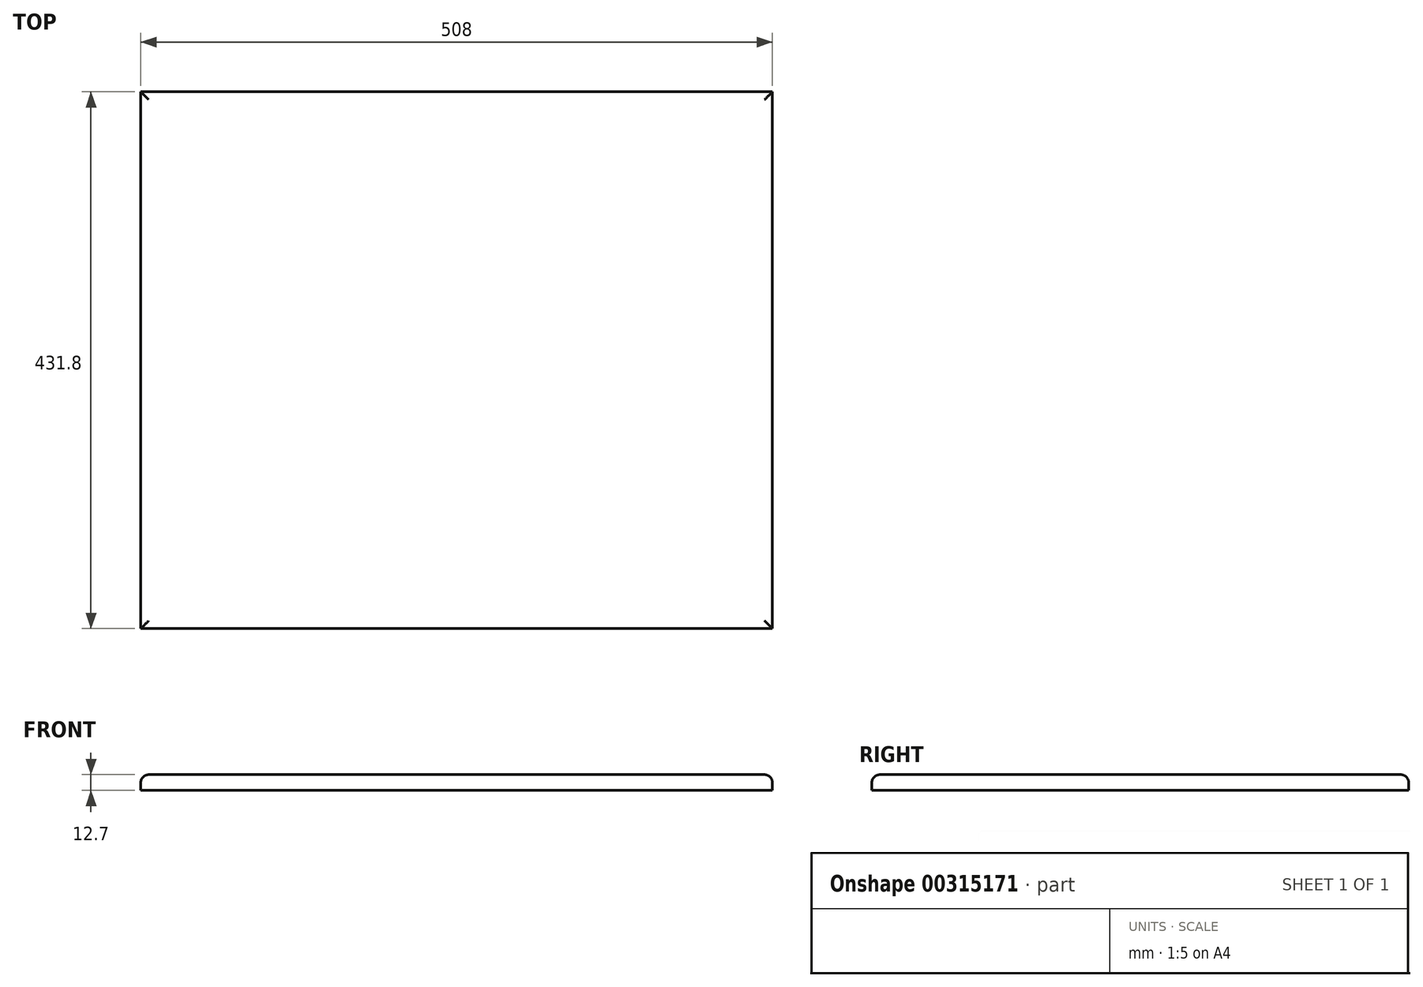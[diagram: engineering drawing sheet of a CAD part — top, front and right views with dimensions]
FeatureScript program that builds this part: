
annotation { "Feature Type Name" : "Feature", "Feature Type Description" : "" }
export const myFeature = defineFeature(function(context is Context, id is Id, definition is map)
    precondition{}
    {
        {
            var Q0;
            Q0=qCreatedBy(makeId("Top.planeOp"),FACE);
            var sketch = newSketch(context, id + "F0", { "sketchPlane" : qUnion([Q0])});
            skLineSegment(sketch, "E0.bottom", {"start": v(-254, -215.9) * mm, "end": v(254, -215.9) * mm});
            skLineSegment(sketch, "E0.top", {"start": v(-254, 215.9) * mm, "end": v(254, 215.9) * mm});
            skLineSegment(sketch, "E0.left", {"start": v(-254, -215.9) * mm, "end": v(-254, 215.9) * mm});
            skLineSegment(sketch, "E0.right", {"start": v(254, -215.9) * mm, "end": v(254, 215.9) * mm});
            skPoint(sketch, "E0.middle", {"position": v(0, 0) * mm});
            skSolve(sketch);
        }
        {
            var Q0;
            Q0=makeQuery(id+"F0.imprint","IMPRINT",FACE,{"disambiguationData":[TD([[makeQuery(id+"F0.imprint","IMPRINT",EDGE,{"derivedFrom":sQuery(id+"F0.wireOp",EDGE,"E0.bottom")}),1.0]])]});
            var Q1;
            Q1=sQuery(id+"F0.wireOp",EDGE,"E0.right");
            var Q2;
            Q2=sQuery(id+"F0.wireOp",EDGE,"E0.top");
            var Q3;
            Q3=sQuery(id+"F0.wireOp",EDGE,"E0.left");
            var Q4;
            Q4=sQuery(id+"F0.wireOp",EDGE,"E0.bottom");
            extrude(context, id + "F1", {"entities" : qUnion([Q0]), "surfaceEntities" : qUnion([Q1, Q2, Q3, Q4]), "depth" : 12.7 * mm});
        }
        {
            var Q0;
            Q0=makeQuery(id+"F1.opExtrude","CAP_FACE",FACE,{"disambiguationData":[OSD([sQuery(id+"F0.wireOp",EDGE,"E0.bottom"),sQuery(id+"F0.wireOp",EDGE,"E0.top"),sQuery(id+"F0.wireOp",EDGE,"E0.left"),sQuery(id+"F0.wireOp",EDGE,"E0.right")])],"isStart":false});
            fillet(context, id + "F2", {"entities" : qUnion([Q0]), "radius" : 6.35 * mm, "tangentPropagation" : true, "allowEdgeOverflow" : false});
        }
    });
